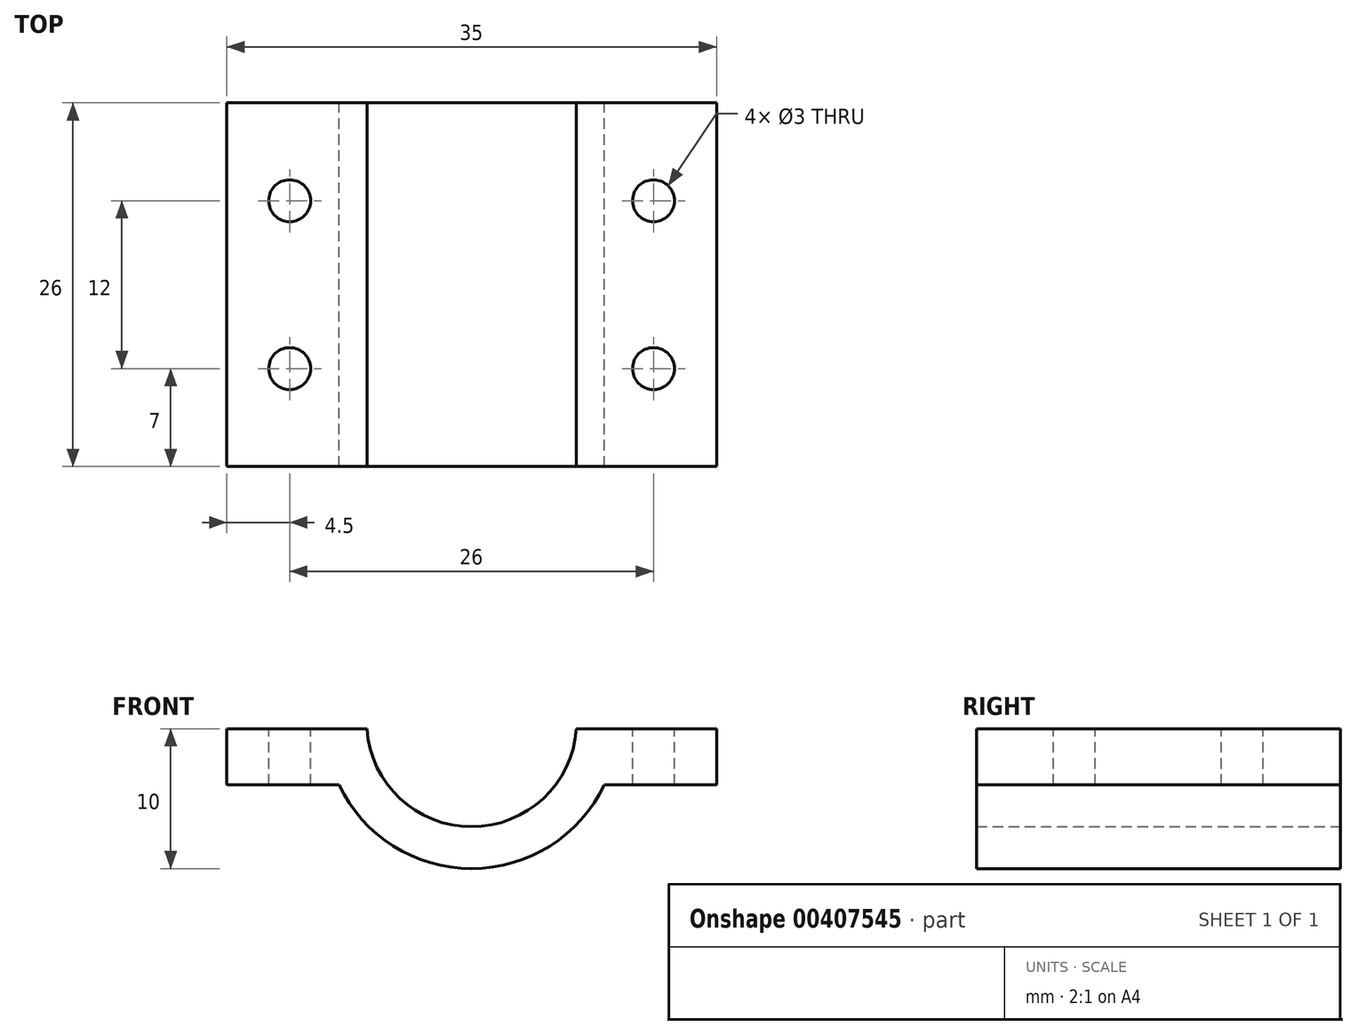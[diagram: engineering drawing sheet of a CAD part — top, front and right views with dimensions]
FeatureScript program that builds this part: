
annotation { "Feature Type Name" : "Feature", "Feature Type Description" : "" }
export const myFeature = defineFeature(function(context is Context, id is Id, definition is map)
    precondition{}
    {
        {
            var Q0;
            Q0=qCreatedBy(makeId("Front.planeOp"),FACE);
            var sketch = newSketch(context, id + "F0", { "sketchPlane" : qUnion([Q0])});
            skArc(sketch, "E0", {"start": v(-7.5, 0) * mm, "mid": v(0, -7.5) * mm, "end": v(7.5, 0) * mm});
            skLineSegment(sketch, "E1", {"start": v(0, 0) * mm, "end": v(-10.5, 0) * mm, "construction": true});
            skLineSegment(sketch, "E2", {"start": v(0, 0) * mm, "end": v(10.5, 0) * mm, "construction": true});
            skLineSegment(sketch, "E3", {"start": v(-7.48, -0.5) * mm, "end": v(-17.5, -0.5) * mm});
            skLineSegment(sketch, "E4", {"start": v(-17.5, -0.5) * mm, "end": v(-17.5, -4.5) * mm});
            skLineSegment(sketch, "E5", {"start": v(-17.5, -4.5) * mm, "end": v(-9.49, -4.5) * mm});
            skLineSegment(sketch, "E6", {"start": v(7.48, -0.5) * mm, "end": v(17.5, -0.5) * mm});
            skLineSegment(sketch, "E7", {"start": v(17.5, -0.5) * mm, "end": v(17.5, -4.5) * mm});
            skLineSegment(sketch, "E8", {"start": v(17.5, -4.5) * mm, "end": v(9.49, -4.5) * mm});
            skArc(sketch, "E9", {"start": v(10.5, 0) * mm, "mid": v(10.5, -0.25) * mm, "end": v(10.49, -0.5) * mm});
            skArc(sketch, "E10.trimOffspring", {"start": v(9.49, -4.5) * mm, "mid": v(0, -10.5) * mm, "end": v(-9.49, -4.5) * mm});
            skArc(sketch, "E11.trimOffspring", {"start": v(-10.49, -0.5) * mm, "mid": v(-10.5, -0.25) * mm, "end": v(-10.5, 0) * mm});
            skSolve(sketch);
        }
        {
            var Q0;
            {var subQ0=sQuery(id+"F0.wireOp",EDGE,"E4");Q0=makeQuery(id+"F0.imprint","IMPRINT",FACE,{"disambiguationData":[TD([[makeQuery(id+"F0.imprint","IMPRINT",EDGE,{"derivedFrom":subQ0}),1.0]])]});}
            extrude(context, id + "F1", {"entities" : qUnion([Q0]), "endBound" : BoundingType.SYMMETRIC, "depth" : 26 * mm});
        }
        {
            var Q0;
            Q0=qCreatedBy(makeId("Top.planeOp"),FACE);
            var sketch = newSketch(context, id + "F2", { "sketchPlane" : qUnion([Q0])});
            skPoint(sketch, "E12.0", {"position": v(-17.5, 0) * mm});
            skPoint(sketch, "E12.1", {"position": v(17.5, 0) * mm});
            skLineSegment(sketch, "E13", {"start": v(17.5, 0) * mm, "end": v(-17.5, 0) * mm, "construction": true});
            skPoint(sketch, "E14", {"position": v(13, 0) * mm});
            skPoint(sketch, "E15", {"position": v(-13, 0) * mm});
            skPoint(sketch, "E16.0", {"position": v(7.5, 0) * mm});
            skPoint(sketch, "E16.1", {"position": v(-7.5, 0) * mm});
            skLineSegment(sketch, "E17", {"start": v(13, -6) * mm, "end": v(13, 6) * mm});
            skLineSegment(sketch, "E18", {"start": v(-13, -6) * mm, "end": v(-13, 6) * mm});
            skCircle(sketch, "E19", {"center": v(13, -6) * mm, "radius": 1.5 * mm});
            skCircle(sketch, "E20", {"center": v(13, 6) * mm, "radius": 1.5 * mm});
            skCircle(sketch, "E21", {"center": v(-13, 6) * mm, "radius": 1.5 * mm});
            skCircle(sketch, "E22", {"center": v(-13, -6) * mm, "radius": 1.5 * mm});
            skCircle(sketch, "E23", {"center": v(13, -6) * mm, "radius": 2.75 * mm, "construction": true});
            skPoint(sketch, "E24.0", {"position": v(9.49, 0) * mm});
            skLineSegment(sketch, "E25", {"start": v(9.49, 0) * mm, "end": v(9.49, -10.63) * mm, "construction": true});
            skSolve(sketch);
        }
        {
            var Q0;
            Q0 = qSketchRegion(id + "F2", true);
            extrude(context, id + "F3", {"entities" : qUnion([Q0]), "operationType" : NewBodyOperationType.REMOVE, "endBound" : BoundingType.THROUGH_ALL, "oppositeDirection" : true, "depth" : 25 * mm});
        }
    });
